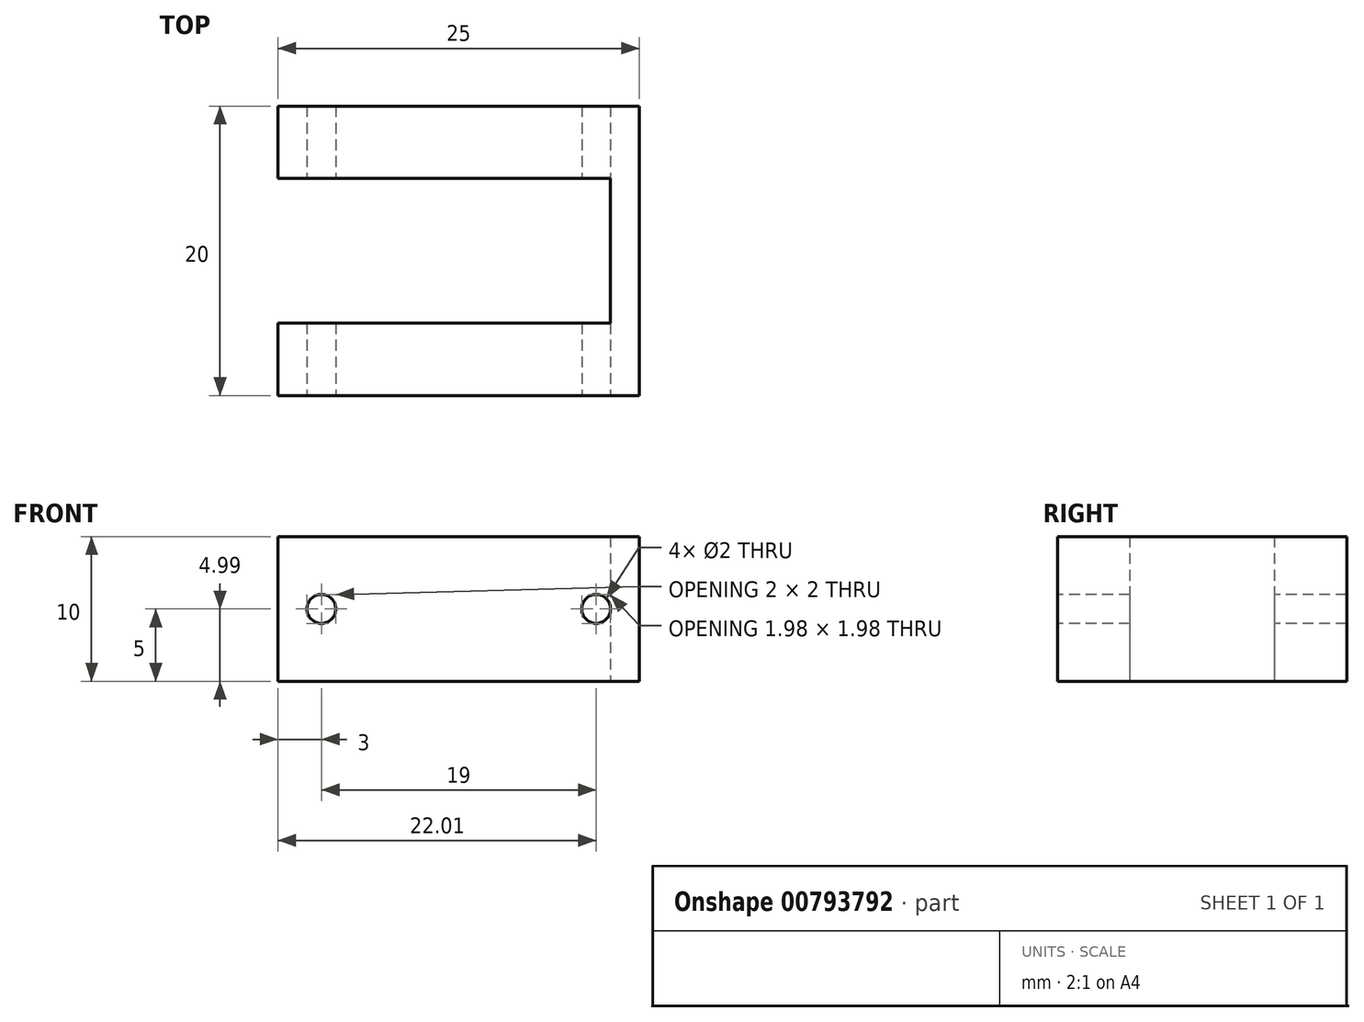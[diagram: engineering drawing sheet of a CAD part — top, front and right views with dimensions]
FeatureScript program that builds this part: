
annotation { "Feature Type Name" : "Feature", "Feature Type Description" : "" }
export const myFeature = defineFeature(function(context is Context, id is Id, definition is map)
    precondition{}
    {
        {
            var Q0;
            Q0=qCreatedBy(makeId("Top.planeOp"),FACE);
            var sketch = newSketch(context, id + "F0", { "sketchPlane" : qUnion([Q0])});
            skLineSegment(sketch, "E0", {"start": v(0, 0) * mm, "end": v(0, -5) * mm});
            skLineSegment(sketch, "E1", {"start": v(0, 0) * mm, "end": v(0, 5) * mm});
            skLineSegment(sketch, "E2", {"start": v(0, 5) * mm, "end": v(15, 5) * mm});
            skLineSegment(sketch, "E3", {"start": v(0, 5) * mm, "end": v(-10, 5) * mm});
            skLineSegment(sketch, "E4", {"start": v(0, -5) * mm, "end": v(15, -5) * mm});
            skLineSegment(sketch, "E5", {"start": v(0, -5) * mm, "end": v(-10, -5) * mm});
            skLineSegment(sketch, "E6", {"start": v(-10, -5) * mm, "end": v(-10, -10) * mm});
            skLineSegment(sketch, "E7", {"start": v(-10, -10) * mm, "end": v(15, -10) * mm});
            skLineSegment(sketch, "E8", {"start": v(15, -10) * mm, "end": v(15, -5) * mm});
            skLineSegment(sketch, "E9", {"start": v(15, 5) * mm, "end": v(15, 10) * mm});
            skLineSegment(sketch, "E10", {"start": v(15, 10) * mm, "end": v(-10, 10) * mm});
            skLineSegment(sketch, "E11", {"start": v(-10, 10) * mm, "end": v(-10, 5) * mm});
            skLineSegment(sketch, "E12.bottom", {"start": v(1, -5) * mm, "end": v(-1, -5) * mm});
            skLineSegment(sketch, "E12.top", {"start": v(1, 5) * mm, "end": v(-1, 5) * mm});
            skPoint(sketch, "E12.middle", {"position": v(0, 0) * mm});
            skLineSegment(sketch, "E13.bottom", {"start": v(15, 5) * mm, "end": v(13, 5) * mm});
            skLineSegment(sketch, "E13.top", {"start": v(15, -5) * mm, "end": v(13, -5) * mm});
            skLineSegment(sketch, "E13.left", {"start": v(15, 5) * mm, "end": v(15, -5) * mm});
            skLineSegment(sketch, "E13.right", {"start": v(13, 5) * mm, "end": v(13, -5) * mm});
            skSolve(sketch);
        }
        {
            var Q0;
            {var subQ6=sQuery(id+"F0.wireOp",EDGE,"E9");Q0=makeQuery(id+"F0.imprint","IMPRINT",FACE,{"disambiguationData":[TD([[makeQuery(id+"F0.imprint","IMPRINT",EDGE,{"derivedFrom":subQ6}),1.0]])]});}
            var Q1;
            {var subQ2=sQuery(id+"F0.wireOp",EDGE,"E6");Q1=makeQuery(id+"F0.imprint","IMPRINT",FACE,{"disambiguationData":[TD([[makeQuery(id+"F0.imprint","IMPRINT",EDGE,{"derivedFrom":subQ2}),1.0]])]});}
            var Q2;
            {var subQ0=sQuery(id+"F0.wireOp",EDGE,"E13.left");Q2=makeQuery(id+"F0.imprint","IMPRINT",FACE,{"disambiguationData":[TD([[makeQuery(id+"F0.imprint","IMPRINT",EDGE,{"derivedFrom":subQ0}),-1.0]])]});}
            extrude(context, id + "F1", {"entities" : qUnion([Q0, Q1, Q2]), "depth" : 10 * mm, "offsetDistance" : 25 * mm});
        }
        {
            var Q0;
            Q0=makeQuery(id+"F1.opExtrude","SWEPT_FACE",FACE,{"disambiguationData":[OSD([sQuery(id+"F0.wireOp",EDGE,"E7")])]});
            var sketch = newSketch(context, id + "F2", { "sketchPlane" : qUnion([Q0])});
            skLineSegment(sketch, "E14", {"start": v(-10, 0) * mm, "end": v(-7, 0) * mm});
            skLineSegment(sketch, "E15", {"start": v(-7, 0) * mm, "end": v(-7, 5) * mm});
            skLineSegment(sketch, "E16", {"start": v(15, 0) * mm, "end": v(12, 0) * mm});
            skLineSegment(sketch, "E17", {"start": v(12, 0) * mm, "end": v(12, 5) * mm});
            skCircle(sketch, "E18", {"center": v(12, 5) * mm, "radius": 1 * mm});
            skCircle(sketch, "E19", {"center": v(-7, 5) * mm, "radius": 1 * mm});
            skSolve(sketch);
        }
        {
            var Q0;
            Q0 = qSketchRegion(id + "F2", true);
            extrude(context, id + "F3", {"entities" : qUnion([Q0]), "operationType" : NewBodyOperationType.REMOVE, "oppositeDirection" : true, "depth" : 20 * mm, "offsetDistance" : 25 * mm});
        }
    });
